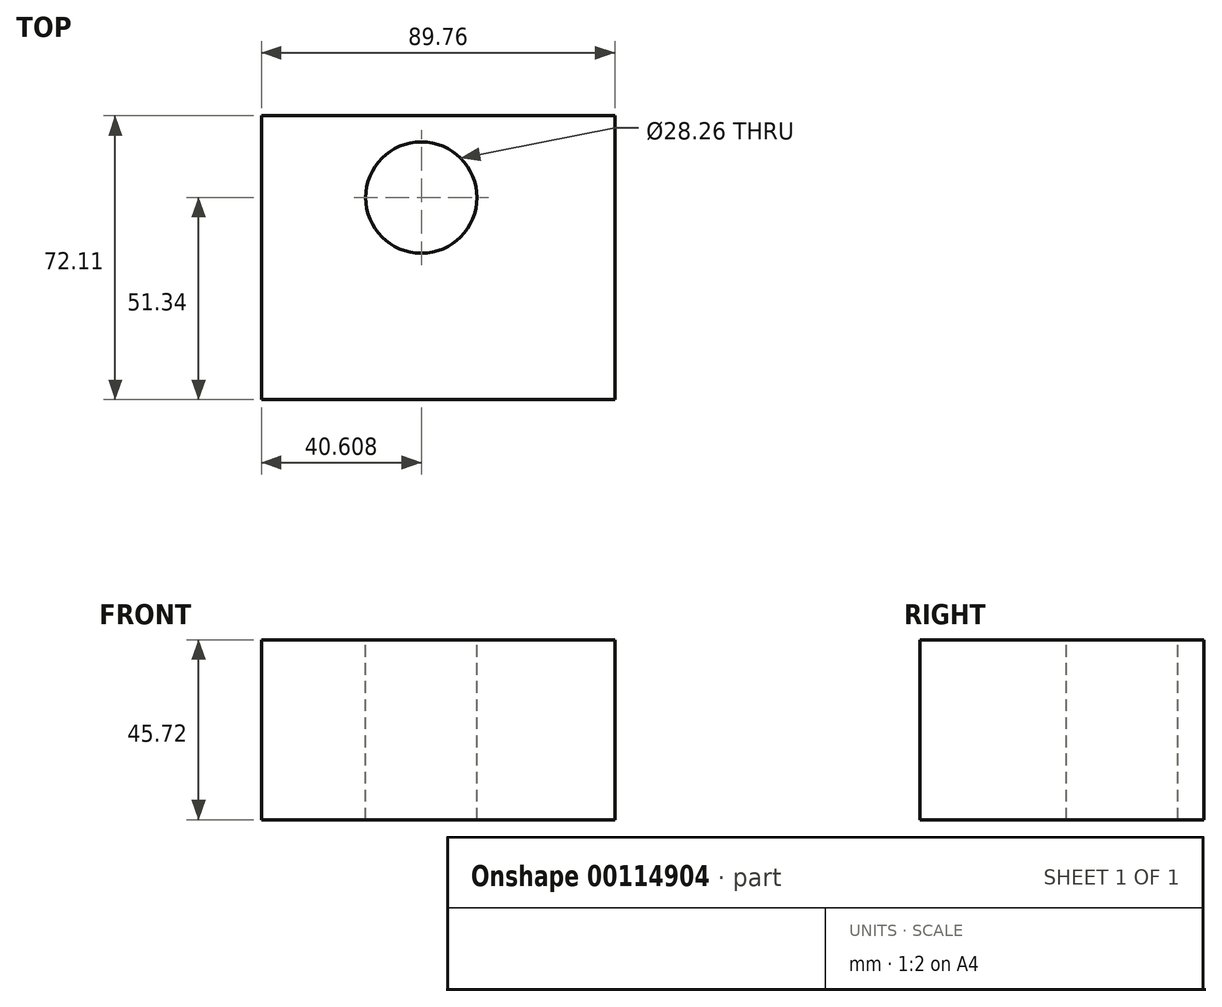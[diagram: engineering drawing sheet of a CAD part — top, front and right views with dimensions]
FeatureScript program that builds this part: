
annotation { "Feature Type Name" : "Feature", "Feature Type Description" : "" }
export const myFeature = defineFeature(function(context is Context, id is Id, definition is map)
    precondition{}
    {
        {
            var Q0;
            Q0=qCreatedBy(makeId("Top.planeOp"),FACE);
            var sketch = newSketch(context, id + "F0", { "sketchPlane" : qUnion([Q0])});
            skLineSegment(sketch, "E0.bottom", {"start": v(-46.25, -35.96) * mm, "end": v(43.51, -35.96) * mm});
            skLineSegment(sketch, "E0.top", {"start": v(-46.25, 36.15) * mm, "end": v(43.51, 36.15) * mm});
            skLineSegment(sketch, "E0.left", {"start": v(-46.25, -35.96) * mm, "end": v(-46.25, 36.15) * mm});
            skLineSegment(sketch, "E0.right", {"start": v(43.51, -35.96) * mm, "end": v(43.51, 36.15) * mm});
            skSolve(sketch);
        }
        {
            var Q0;
            Q0 = qSketchRegion(id + "F0", true);
            extrude(context, id + "F1", {"entities" : qUnion([Q0]), "endBound" : BoundingType.SYMMETRIC, "depth" : 45.72 * mm});
        }
        {
            var Q0;
            Q0=makeQuery(id+"F1.opExtrude","CAP_FACE",FACE,{"disambiguationData":[OSD([sQuery(id+"F0.wireOp",EDGE,"E0.bottom"),sQuery(id+"F0.wireOp",EDGE,"E0.top"),sQuery(id+"F0.wireOp",EDGE,"E0.left"),sQuery(id+"F0.wireOp",EDGE,"E0.right")])],"isStart":false});
            var sketch = newSketch(context, id + "F2", { "sketchPlane" : qUnion([Q0])});
            skCircle(sketch, "E1", {"center": v(-5.64, 15.38) * mm, "radius": 14.13 * mm});
            skSolve(sketch);
        }
        {
            var Q0;
            Q0 = qSketchRegion(id + "F2", true);
            extrude(context, id + "F3", {"entities" : qUnion([Q0]), "operationType" : NewBodyOperationType.REMOVE, "endBound" : BoundingType.UP_TO_NEXT, "oppositeDirection" : true, "depth" : 25.4 * mm});
        }
    });
